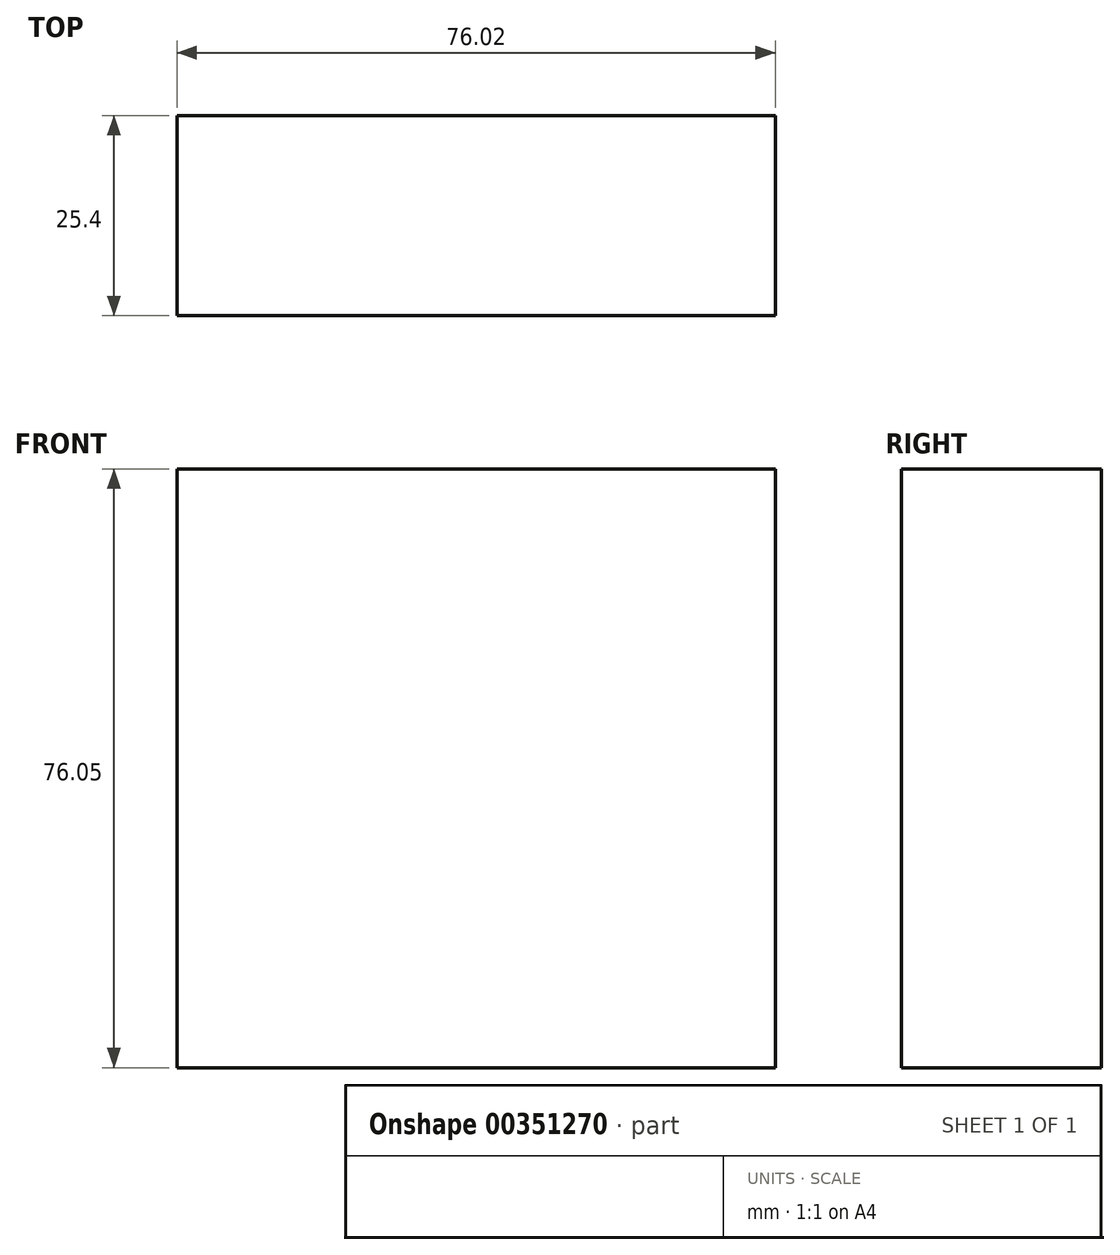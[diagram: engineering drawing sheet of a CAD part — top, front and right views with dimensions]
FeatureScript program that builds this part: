
annotation { "Feature Type Name" : "Feature", "Feature Type Description" : "" }
export const myFeature = defineFeature(function(context is Context, id is Id, definition is map)
    precondition{}
    {
        {
            var Q0;
            Q0=qCreatedBy(makeId("Front.planeOp"),FACE);
            var sketch = newSketch(context, id + "F0", { "sketchPlane" : qUnion([Q0])});
            skLineSegment(sketch, "E0.bottom", {"start": v(-76.02, 76.05) * mm, "end": v(0, 76.05) * mm});
            skLineSegment(sketch, "E0.top", {"start": v(-76.02, 0) * mm, "end": v(0, 0) * mm});
            skLineSegment(sketch, "E0.left", {"start": v(-76.02, 76.05) * mm, "end": v(-76.02, 0) * mm});
            skLineSegment(sketch, "E0.right", {"start": v(0, 76.05) * mm, "end": v(0, 0) * mm});
            skSolve(sketch);
        }
        {
            var Q0;
            Q0=makeQuery(id+"F0.imprint","IMPRINT",FACE,{"disambiguationData":[TD([[makeQuery(id+"F0.imprint","IMPRINT",EDGE,{"derivedFrom":sQuery(id+"F0.wireOp",EDGE,"E0.bottom")}),-1.0]])]});
            extrude(context, id + "F1", {"entities" : qUnion([Q0]), "depth" : 25.4 * mm});
        }
    });
